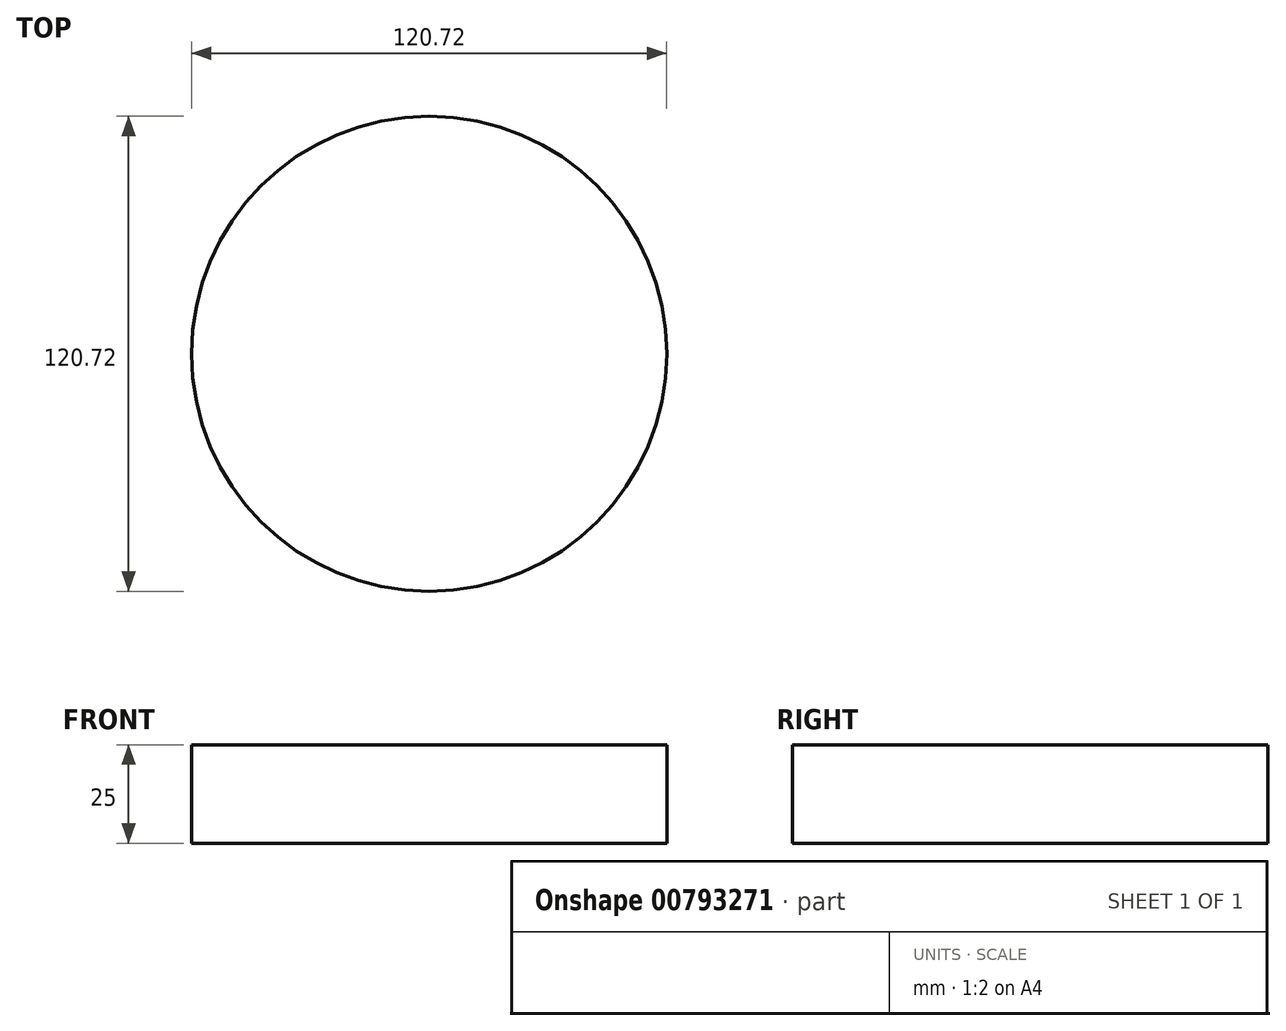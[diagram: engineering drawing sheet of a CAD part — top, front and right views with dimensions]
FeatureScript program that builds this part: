
annotation { "Feature Type Name" : "Feature", "Feature Type Description" : "" }
export const myFeature = defineFeature(function(context is Context, id is Id, definition is map)
    precondition{}
    {
        {
            var Q0;
            Q0=qCreatedBy(makeId("Top.planeOp"),FACE);
            var sketch = newSketch(context, id + "F0", { "sketchPlane" : qUnion([Q0])});
            skCircle(sketch, "E0", {"center": v(0, 0) * mm, "radius": 60.36 * mm});
            skSolve(sketch);
        }
        {
            var Q0;
            Q0=makeQuery(id+"F0.imprint","IMPRINT",FACE,{"disambiguationData":[TD([[makeQuery(id+"F0.imprint","IMPRINT",EDGE,{"derivedFrom":sQuery(id+"F0.wireOp",EDGE,"E0")}),1.0]])]});
            extrude(context, id + "F1", {"entities" : qUnion([Q0]), "depth" : 25 * mm, "offsetDistance" : 25 * mm});
        }
    });
